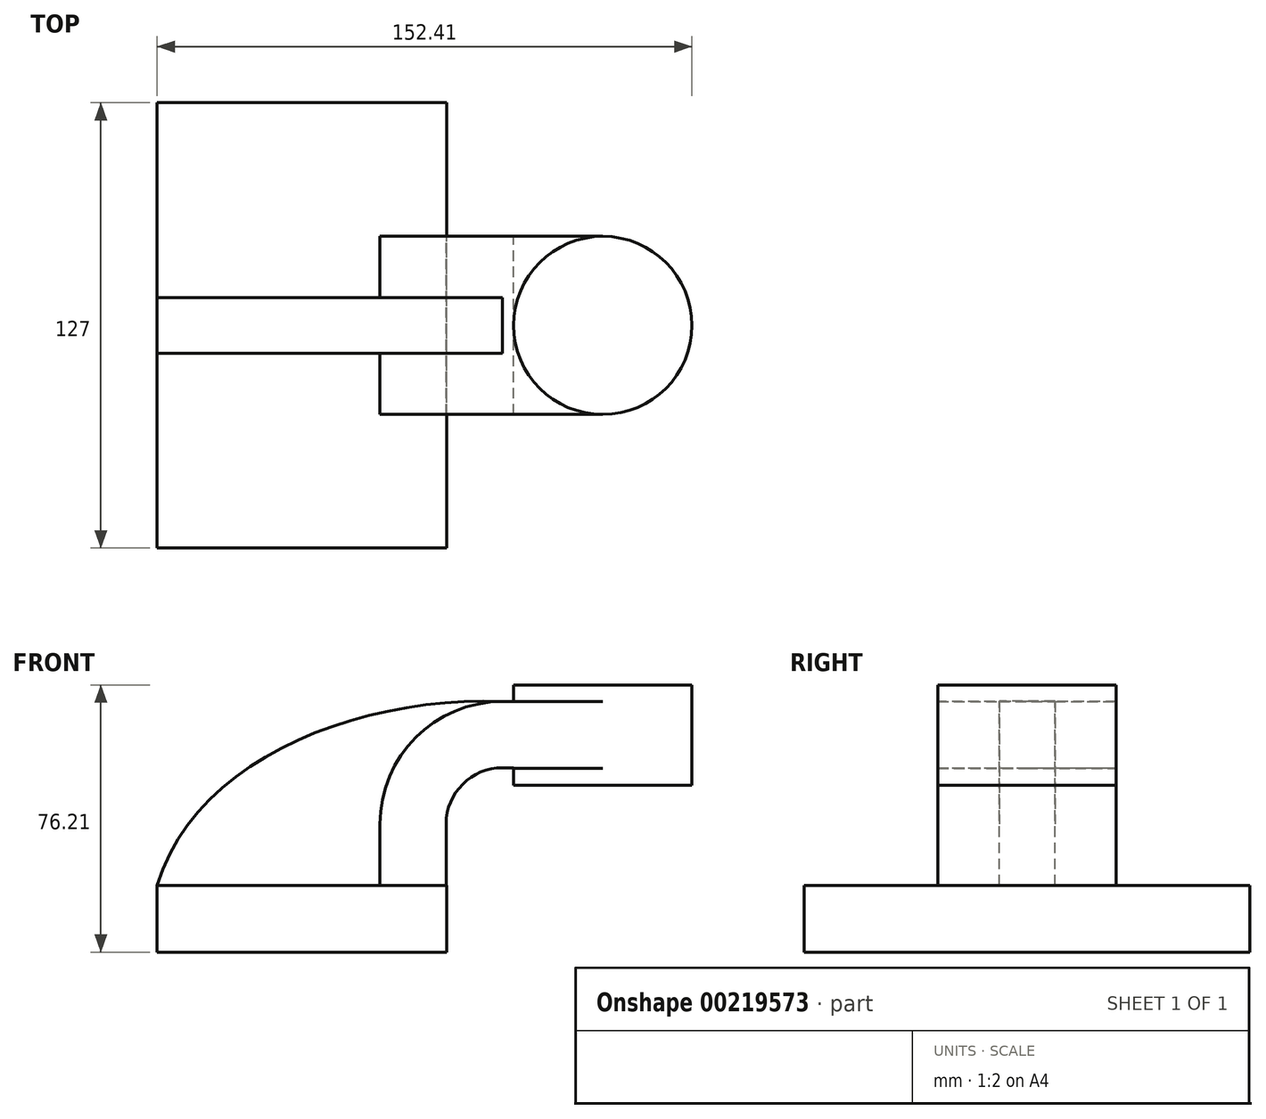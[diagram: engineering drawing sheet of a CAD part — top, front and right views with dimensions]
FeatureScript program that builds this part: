
annotation { "Feature Type Name" : "Feature", "Feature Type Description" : "" }
export const myFeature = defineFeature(function(context is Context, id is Id, definition is map)
    precondition{}
    {
        {
            var Q0;
            Q0=qCreatedBy(makeId("Front.planeOp"),FACE);
            var sketch = newSketch(context, id + "F0", { "sketchPlane" : qUnion([Q0])});
            skLineSegment(sketch, "E0.bottom", {"start": v(41.28, -9.52) * mm, "end": v(-41.28, -9.53) * mm});
            skLineSegment(sketch, "E0.top", {"start": v(41.28, 9.53) * mm, "end": v(-41.28, 9.53) * mm});
            skLineSegment(sketch, "E0.left", {"start": v(41.28, -9.52) * mm, "end": v(41.28, 9.53) * mm});
            skLineSegment(sketch, "E0.right", {"start": v(-41.28, -9.53) * mm, "end": v(-41.28, 9.53) * mm});
            skPoint(sketch, "E0.middle", {"position": v(0, 0) * mm});
            skLineSegment(sketch, "E1.bottom", {"start": v(111.12, 38.1) * mm, "end": v(60.32, 38.1) * mm});
            skLineSegment(sketch, "E1.top", {"start": v(111.12, 66.68) * mm, "end": v(60.32, 66.68) * mm});
            skLineSegment(sketch, "E1.left", {"start": v(111.12, 38.1) * mm, "end": v(111.12, 66.68) * mm});
            skLineSegment(sketch, "E1.right", {"start": v(60.32, 38.1) * mm, "end": v(60.32, 66.67) * mm});
            skPoint(sketch, "E1.middle", {"position": v(85.72, 52.39) * mm});
            skLineSegment(sketch, "E2", {"start": v(41.28, 9.53) * mm, "end": v(41.28, 27) * mm});
            skArc(sketch, "E3", {"start": v(57.15, 42.88) * mm, "mid": v(45.92, 38.23) * mm, "end": v(41.27, 27) * mm});
            skLineSegment(sketch, "E4", {"start": v(57.15, 42.88) * mm, "end": v(85.72, 42.88) * mm});
            skLineSegment(sketch, "E5.0", {"start": v(41.1, 9.53) * mm, "end": v(41.1, 27) * mm});
            skArc(sketch, "E5.1", {"start": v(57.15, 43.06) * mm, "mid": v(45.8, 38.36) * mm, "end": v(41.1, 27) * mm});
            skLineSegment(sketch, "E5.2", {"start": v(57.15, 43.06) * mm, "end": v(85.5, 43.06) * mm});
            skLineSegment(sketch, "E6.0", {"start": v(57.15, 61.93) * mm, "end": v(85.72, 61.93) * mm});
            skArc(sketch, "E6.1", {"start": v(57.15, 61.93) * mm, "mid": v(32.45, 51.7) * mm, "end": v(22.23, 27) * mm});
            skLineSegment(sketch, "E6.2", {"start": v(22.23, 9.53) * mm, "end": v(22.23, 27) * mm});
            skLineSegment(sketch, "E7", {"start": v(85.72, 38.1) * mm, "end": v(85.72, 66.68) * mm});
            skFitSpline(sketch, "E8", {"points": [v(-41.28, 9.53) * mm, v(57.15, 61.93) * mm], "startDerivative": vector(32.44, 107.7) * mm, "endDerivative": vector(124.66, -4.73) * mm});
            skSolve(sketch);
        }
        {
            var Q0;
            Q0=makeQuery(id+"F0.imprint","IMPRINT",FACE,{"disambiguationData":[TD([[makeQuery(id+"F0.imprint","IMPRINT",EDGE,{"derivedFrom":sQuery(id+"F0.wireOp",EDGE,"E0.bottom")}),-1.0]])]});
            extrude(context, id + "F1", {"entities" : qUnion([Q0]), "endBound" : BoundingType.SYMMETRIC, "depth" : 127 * mm});
        }
        {
            var Q0;
            {var subQ1=sQuery(id+"F0.wireOp",EDGE,"E5.0");Q0=makeQuery(id+"F0.imprint","IMPRINT",FACE,{"disambiguationData":[TD([[makeQuery(id+"F0.imprint","IMPRINT",EDGE,{"derivedFrom":subQ1}),1.0]])]});}
            var Q1;
            {var subQ3=sQuery(id+"F0.wireOp",EDGE,"E1.right");var subQ5=sQuery(id+"F0.wireOp",EDGE,"E4");var subQ7=makeQuery(id+"F0.imprint","INTERSECT",VERTEX,{"derivedFrom":[subQ3,subQ5]});Q1=makeQuery(id+"F0.imprint","IMPRINT",FACE,{"disambiguationData":[TD([[makeQuery(id+"F0.imprint","IMPRINT",EDGE,{"disambiguationData":[TD([[subQ7,-1.0]])],"derivedFrom":subQ3}),-1.0]])]});}
            extrude(context, id + "F2", {"entities" : qUnion([Q0, Q1]), "operationType" : NewBodyOperationType.ADD, "endBound" : BoundingType.SYMMETRIC, "depth" : 50.8 * mm});
        }
        {
            var Q0;
            Q0=makeQuery(id+"F0.imprint","IMPRINT",FACE,{"disambiguationData":[TD([[makeQuery(id+"F0.imprint","IMPRINT",EDGE,{"derivedFrom":sQuery(id+"F0.wireOp",EDGE,"E6.1")}),-1.0]])]});
            extrude(context, id + "F3", {"entities" : qUnion([Q0]), "operationType" : NewBodyOperationType.ADD, "endBound" : BoundingType.SYMMETRIC, "depth" : 15.88 * mm});
        }
        {
            var Q0;
            {var subQ4=sQuery(id+"F0.wireOp",EDGE,"E1.left");Q0=makeQuery(id+"F0.imprint","IMPRINT",FACE,{"disambiguationData":[TD([[makeQuery(id+"F0.imprint","IMPRINT",EDGE,{"derivedFrom":subQ4}),1.0]])]});}
            var Q1;
            Q1=sQuery(id+"F0.wireOp",EDGE,"E7");
            revolve(context, id + "F4", {"operationType" : NewBodyOperationType.ADD, "entities" : qUnion([Q0]), "axis" : qUnion([Q1]), "revolveType" : RevolveType.FULL});
        }
    });
